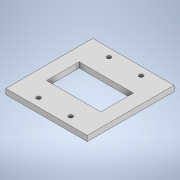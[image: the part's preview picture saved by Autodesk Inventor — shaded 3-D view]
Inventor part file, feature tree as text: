
AUTODESK INVENTOR PART (.ipt)
format: ipt  version: 2022 (Build 260153000, 153)  size: 115,712 bytes
history: native  units: mm
features: extrude x1, sketch x1
ambient origin geometry x8: Origin, YZ Plane, XZ Plane, XY Plane, X Axis, Y Axis, Z Axis, Center Point
bodies: Solid1 (feature_tree)
feature tree (2):
  extrude  "Extrusion1"  Depth=16.0mm
  sketch  "Sketch1"  dims[d0=15.0mm d1=16.0mm d2=10.0mm d3=6.0mm d4=2.5mm d5=5.0mm d6=0.75mm d7=4.5125mm d8=1.5mm d9=20.0mm d11=5.925mm d12=20.0mm d14=12.985mm d17=1.0mm d18=0.0mm]
